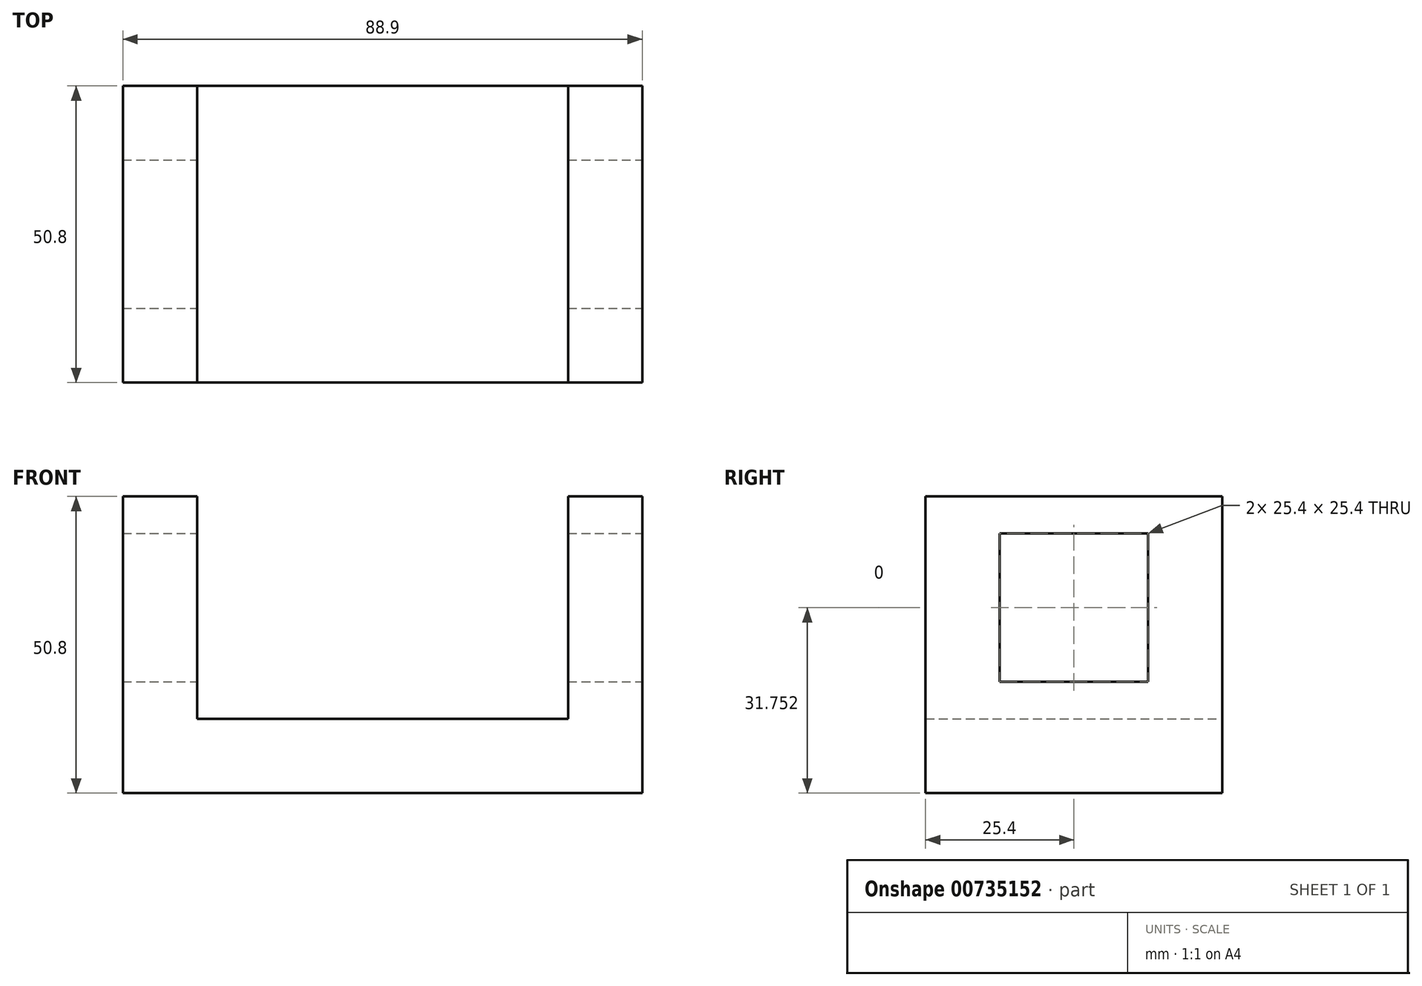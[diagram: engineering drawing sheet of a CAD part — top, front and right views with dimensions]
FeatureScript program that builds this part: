
annotation { "Feature Type Name" : "Feature", "Feature Type Description" : "" }
export const myFeature = defineFeature(function(context is Context, id is Id, definition is map)
    precondition{}
    {
        {
            var Q0;
            Q0=qCreatedBy(makeId("Front.planeOp"),FACE);
            var sketch = newSketch(context, id + "F0", { "sketchPlane" : qUnion([Q0])});
            skLineSegment(sketch, "E0", {"start": v(-42.45, 27.2) * mm, "end": v(-29.75, 27.2) * mm});
            skLineSegment(sketch, "E1", {"start": v(-42.45, 27.2) * mm, "end": v(-42.45, -23.6) * mm});
            skLineSegment(sketch, "E2", {"start": v(-42.45, -23.6) * mm, "end": v(46.45, -23.6) * mm});
            skLineSegment(sketch, "E3", {"start": v(46.45, -23.6) * mm, "end": v(46.45, 27.2) * mm});
            skLineSegment(sketch, "E4", {"start": v(46.45, 27.2) * mm, "end": v(33.75, 27.2) * mm});
            skLineSegment(sketch, "E5", {"start": v(33.75, 27.2) * mm, "end": v(33.75, -10.9) * mm});
            skLineSegment(sketch, "E6", {"start": v(-29.75, 27.2) * mm, "end": v(-29.75, -10.9) * mm});
            skLineSegment(sketch, "E7", {"start": v(33.75, -10.9) * mm, "end": v(-29.75, -10.9) * mm});
            skSolve(sketch);
        }
        {
            var Q0;
            Q0=makeQuery(id+"F0.imprint","IMPRINT",FACE,{"disambiguationData":[TD([[makeQuery(id+"F0.imprint","IMPRINT",EDGE,{"derivedFrom":sQuery(id+"F0.wireOp",EDGE,"E0")}),-1.0]])]});
            extrude(context, id + "F1", {"entities" : qUnion([Q0]), "depth" : 50.8 * mm, "offsetDistance" : 25.4 * mm});
        }
        {
            var Q0;
            Q0=makeQuery(id+"F1.opExtrude","SWEPT_FACE",FACE,{"disambiguationData":[OSD([sQuery(id+"F0.wireOp",EDGE,"E3")])]});
            var sketch = newSketch(context, id + "F2", { "sketchPlane" : qUnion([Q0])});
            skLineSegment(sketch, "E8.bottom", {"start": v(-38.1, 20.84) * mm, "end": v(-12.7, 20.84) * mm});
            skLineSegment(sketch, "E8.top", {"start": v(-38.1, -4.56) * mm, "end": v(-12.7, -4.56) * mm});
            skLineSegment(sketch, "E8.left", {"start": v(-38.1, 20.84) * mm, "end": v(-38.1, -4.56) * mm});
            skLineSegment(sketch, "E8.right", {"start": v(-12.7, 20.84) * mm, "end": v(-12.7, -4.56) * mm});
            skSolve(sketch);
        }
        {
            var Q0;
            Q0=makeQuery(id+"F2.imprint","IMPRINT",FACE,{"disambiguationData":[TD([[makeQuery(id+"F2.imprint","IMPRINT",EDGE,{"derivedFrom":sQuery(id+"F2.wireOp",EDGE,"E8.bottom")}),-1.0]])]});
            extrude(context, id + "F3", {"entities" : qUnion([Q0]), "operationType" : NewBodyOperationType.REMOVE, "endBound" : BoundingType.THROUGH_ALL, "oppositeDirection" : true, "depth" : 25.4 * mm, "offsetDistance" : 25.4 * mm});
        }
    });
